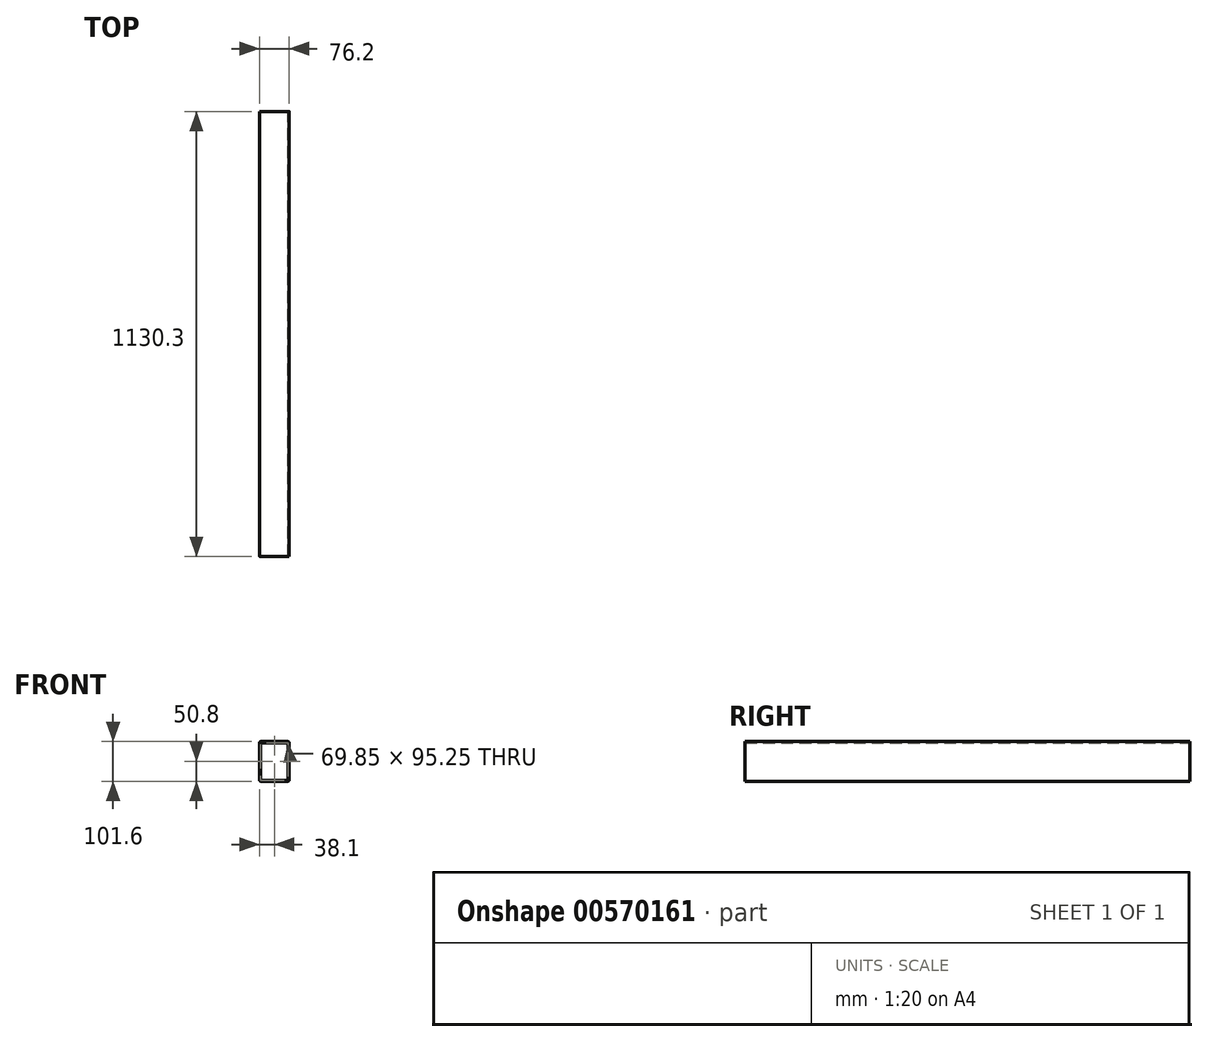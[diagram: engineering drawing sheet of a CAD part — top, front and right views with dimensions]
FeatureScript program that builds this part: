
annotation { "Feature Type Name" : "Feature", "Feature Type Description" : "" }
export const myFeature = defineFeature(function(context is Context, id is Id, definition is map)
    precondition{}
    {
        {
            var Q0;
            Q0=qCreatedBy(makeId("Front.planeOp"),FACE);
            var sketch = newSketch(context, id + "F0", { "sketchPlane" : qUnion([Q0])});
            skLineSegment(sketch, "E0.bottom", {"start": v(0, 0) * mm, "end": v(76.2, 0) * mm});
            skLineSegment(sketch, "E0.top", {"start": v(0, 101.6) * mm, "end": v(76.2, 101.6) * mm});
            skLineSegment(sketch, "E0.left", {"start": v(0, 0) * mm, "end": v(0, 101.6) * mm});
            skLineSegment(sketch, "E0.right", {"start": v(76.2, 0) * mm, "end": v(76.2, 101.6) * mm});
            skLineSegment(sketch, "E1.bottom", {"start": v(3.17, 3.18) * mm, "end": v(73.03, 3.18) * mm});
            skLineSegment(sketch, "E1.top", {"start": v(3.17, 98.42) * mm, "end": v(73.02, 98.42) * mm});
            skLineSegment(sketch, "E1.left", {"start": v(3.17, 3.18) * mm, "end": v(3.17, 98.42) * mm});
            skLineSegment(sketch, "E1.right", {"start": v(73.03, 3.18) * mm, "end": v(73.02, 98.42) * mm});
            skSolve(sketch);
        }
        {
            var Q0;
            Q0=makeQuery(id+"F0.imprint","IMPRINT",FACE,{"disambiguationData":[TD([[makeQuery(id+"F0.imprint","IMPRINT",EDGE,{"derivedFrom":sQuery(id+"F0.wireOp",EDGE,"E0.bottom")}),1.0]])]});
            extrude(context, id + "F1", {"entities" : qUnion([Q0]), "depth" : 1130.3 * mm, "offsetDistance" : 25.4 * mm});
        }
        {
            var Q0;
            Q0=makeQuery(id+"F1.opExtrude","SWEPT_EDGE",EDGE,{"disambiguationData":[OSD([sQuery(id+"F0.wireOp",EDGE,"E0.top"),sQuery(id+"F0.wireOp",EDGE,"E0.left")])]});
            var Q1;
            Q1=makeQuery(id+"F1.opExtrude","SWEPT_EDGE",EDGE,{"disambiguationData":[OSD([sQuery(id+"F0.wireOp",EDGE,"E0.bottom"),sQuery(id+"F0.wireOp",EDGE,"E0.left")])]});
            var Q2;
            Q2=makeQuery(id+"F1.opExtrude","SWEPT_EDGE",EDGE,{"disambiguationData":[OSD([sQuery(id+"F0.wireOp",EDGE,"E0.top"),sQuery(id+"F0.wireOp",EDGE,"E0.right")])]});
            var Q3;
            Q3=makeQuery(id+"F1.opExtrude","SWEPT_EDGE",EDGE,{"disambiguationData":[OSD([sQuery(id+"F0.wireOp",EDGE,"E0.bottom"),sQuery(id+"F0.wireOp",EDGE,"E0.right")])]});
            fillet(context, id + "F2", {"entities" : qUnion([Q0, Q1, Q2, Q3]), "radius" : 5.08 * mm, "tangentPropagation" : true, "allowEdgeOverflow" : false});
        }
    });
